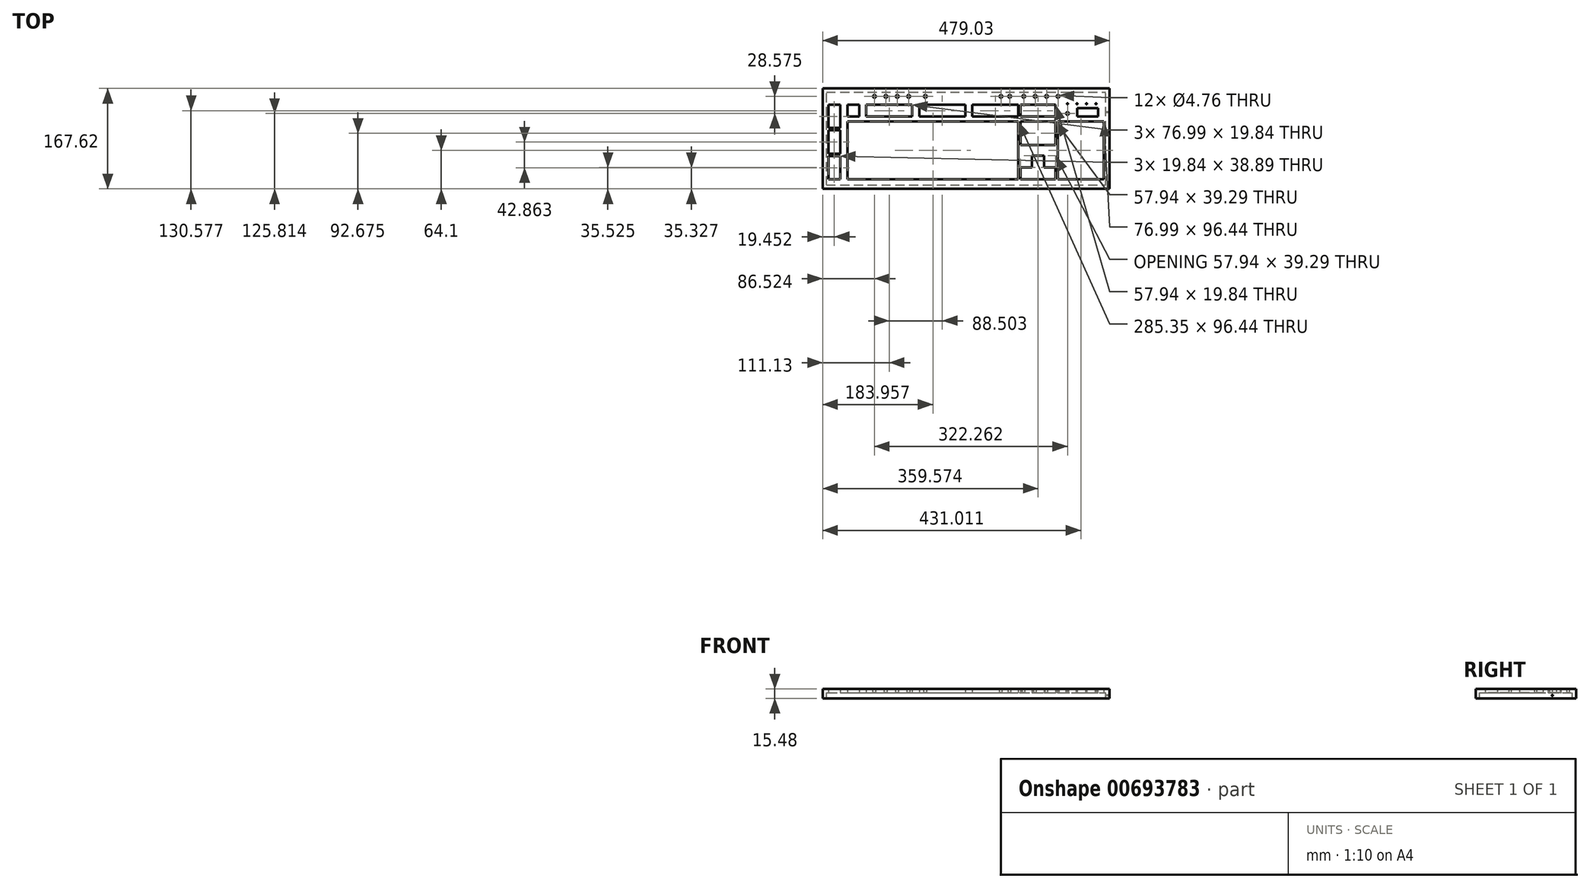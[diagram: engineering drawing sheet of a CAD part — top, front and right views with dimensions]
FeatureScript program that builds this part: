
annotation { "Feature Type Name" : "Feature", "Feature Type Description" : "" }
export const myFeature = defineFeature(function(context is Context, id is Id, definition is map)
    precondition{}
    {
        {
            var Q0;
            Q0=qCreatedBy(makeId("Top.planeOp"),FACE);
            var sketch = newSketch(context, id + "F0", { "sketchPlane" : qUnion([Q0])});
            skLineSegment(sketch, "E0.bottom", {"start": v(6.35, 6.35) * mm, "end": v(26.2, 6.35) * mm});
            skLineSegment(sketch, "E0.top", {"start": v(6.35, 45.24) * mm, "end": v(26.2, 45.24) * mm});
            skLineSegment(sketch, "E0.left", {"start": v(6.35, 6.35) * mm, "end": v(6.35, 45.24) * mm});
            skLineSegment(sketch, "E0.right", {"start": v(26.2, 6.35) * mm, "end": v(26.2, 45.24) * mm});
            skLineSegment(sketch, "E1.bottom", {"start": v(6.35, 49.21) * mm, "end": v(26.2, 49.21) * mm});
            skLineSegment(sketch, "E1.top", {"start": v(6.35, 88.1) * mm, "end": v(26.2, 88.1) * mm});
            skLineSegment(sketch, "E1.left", {"start": v(6.35, 49.21) * mm, "end": v(6.35, 88.1) * mm});
            skLineSegment(sketch, "E1.right", {"start": v(26.2, 49.21) * mm, "end": v(26.2, 88.1) * mm});
            skLineSegment(sketch, "E2.bottom", {"start": v(6.35, 92.08) * mm, "end": v(26.2, 92.08) * mm});
            skLineSegment(sketch, "E2.top", {"start": v(6.35, 130.97) * mm, "end": v(26.2, 130.97) * mm});
            skLineSegment(sketch, "E2.left", {"start": v(6.35, 92.08) * mm, "end": v(6.35, 130.97) * mm});
            skLineSegment(sketch, "E2.right", {"start": v(26.2, 92.08) * mm, "end": v(26.2, 130.97) * mm});
            skLineSegment(sketch, "E3.bottom", {"start": v(38.1, 130.97) * mm, "end": v(57.94, 130.97) * mm});
            skLineSegment(sketch, "E3.top", {"start": v(38.1, 111.13) * mm, "end": v(57.94, 111.13) * mm});
            skLineSegment(sketch, "E3.left", {"start": v(38.1, 130.97) * mm, "end": v(38.1, 111.13) * mm});
            skLineSegment(sketch, "E3.right", {"start": v(57.94, 130.97) * mm, "end": v(57.94, 111.13) * mm});
            skLineSegment(sketch, "E4.bottom", {"start": v(69.45, 111.13) * mm, "end": v(146.45, 111.13) * mm});
            skLineSegment(sketch, "E4.top", {"start": v(69.45, 130.97) * mm, "end": v(146.45, 130.97) * mm});
            skLineSegment(sketch, "E4.left", {"start": v(69.45, 111.13) * mm, "end": v(69.45, 130.97) * mm});
            skLineSegment(sketch, "E4.right", {"start": v(146.45, 111.13) * mm, "end": v(146.45, 130.97) * mm});
            skLineSegment(sketch, "E5.bottom", {"start": v(157.96, 130.97) * mm, "end": v(234.95, 130.97) * mm});
            skLineSegment(sketch, "E5.top", {"start": v(157.96, 111.13) * mm, "end": v(234.95, 111.13) * mm});
            skLineSegment(sketch, "E5.left", {"start": v(157.96, 130.97) * mm, "end": v(157.96, 111.13) * mm});
            skLineSegment(sketch, "E5.right", {"start": v(234.95, 130.97) * mm, "end": v(234.95, 111.13) * mm});
            skLineSegment(sketch, "E6.bottom", {"start": v(246.46, 111.13) * mm, "end": v(323.45, 111.13) * mm});
            skLineSegment(sketch, "E6.top", {"start": v(246.46, 130.97) * mm, "end": v(323.45, 130.97) * mm});
            skLineSegment(sketch, "E6.left", {"start": v(246.46, 111.13) * mm, "end": v(246.46, 130.97) * mm});
            skLineSegment(sketch, "E6.right", {"start": v(323.45, 111.13) * mm, "end": v(323.45, 130.97) * mm});
            skLineSegment(sketch, "E7.bottom", {"start": v(38.1, 6.35) * mm, "end": v(323.45, 6.35) * mm});
            skLineSegment(sketch, "E7.top", {"start": v(38.1, 102.8) * mm, "end": v(323.45, 102.8) * mm});
            skLineSegment(sketch, "E7.left", {"start": v(38.1, 6.35) * mm, "end": v(38.1, 102.8) * mm});
            skLineSegment(sketch, "E7.right", {"start": v(323.45, 6.35) * mm, "end": v(323.45, 102.8) * mm});
            skLineSegment(sketch, "E8.bottom", {"start": v(327.42, 111.13) * mm, "end": v(385.37, 111.13) * mm});
            skLineSegment(sketch, "E8.top", {"start": v(327.42, 130.97) * mm, "end": v(385.37, 130.97) * mm});
            skLineSegment(sketch, "E8.left", {"start": v(327.42, 111.13) * mm, "end": v(327.42, 130.97) * mm});
            skLineSegment(sketch, "E8.right", {"start": v(385.37, 111.13) * mm, "end": v(385.37, 130.97) * mm});
            skLineSegment(sketch, "E9.bottom", {"start": v(327.42, 102.8) * mm, "end": v(385.37, 102.8) * mm});
            skLineSegment(sketch, "E9.top", {"start": v(327.42, 63.5) * mm, "end": v(385.37, 63.5) * mm});
            skLineSegment(sketch, "E9.left", {"start": v(327.42, 102.8) * mm, "end": v(327.42, 63.5) * mm});
            skLineSegment(sketch, "E9.right", {"start": v(385.37, 102.8) * mm, "end": v(385.37, 63.5) * mm});
            skLineSegment(sketch, "E10", {"start": v(327.42, 6.35) * mm, "end": v(327.42, 26.2) * mm});
            skLineSegment(sketch, "E11", {"start": v(327.42, 26.2) * mm, "end": v(346.47, 26.2) * mm});
            skLineSegment(sketch, "E12", {"start": v(346.47, 26.2) * mm, "end": v(346.47, 45.64) * mm});
            skLineSegment(sketch, "E13", {"start": v(346.47, 45.64) * mm, "end": v(366.32, 45.64) * mm});
            skLineSegment(sketch, "E14", {"start": v(366.32, 45.64) * mm, "end": v(366.32, 26.2) * mm});
            skLineSegment(sketch, "E15", {"start": v(366.32, 26.2) * mm, "end": v(385.37, 26.2) * mm});
            skLineSegment(sketch, "E16", {"start": v(385.37, 26.2) * mm, "end": v(385.37, 6.35) * mm});
            skLineSegment(sketch, "E17", {"start": v(385.37, 6.35) * mm, "end": v(327.42, 6.35) * mm});
            skPoint(sketch, "E18", {"position": v(356.4, 6.35) * mm});
            skPoint(sketch, "E19", {"position": v(356.4, 45.64) * mm});
            skLineSegment(sketch, "E20.bottom", {"start": v(389.33, 6.35) * mm, "end": v(466.33, 6.35) * mm});
            skLineSegment(sketch, "E20.top", {"start": v(389.33, 102.8) * mm, "end": v(466.33, 102.8) * mm});
            skLineSegment(sketch, "E20.left", {"start": v(389.33, 6.35) * mm, "end": v(389.33, 102.8) * mm});
            skLineSegment(sketch, "E20.right", {"start": v(466.33, 6.35) * mm, "end": v(466.33, 102.8) * mm});
            skLineSegment(sketch, "E21.bottom", {"start": v(-3.18, -9.53) * mm, "end": v(475.85, -9.52) * mm});
            skLineSegment(sketch, "E21.top", {"start": v(-3.18, 158.1) * mm, "end": v(475.85, 158.1) * mm});
            skLineSegment(sketch, "E21.left", {"start": v(-3.18, -9.53) * mm, "end": v(-3.18, 158.1) * mm});
            skLineSegment(sketch, "E21.right", {"start": v(475.85, -9.52) * mm, "end": v(475.85, 158.1) * mm});
            skSolve(sketch);
        }
        {
            var Q0;
            Q0 = qSketchRegion(id + "F0", true);
            extrude(context, id + "F1", {"entities" : qUnion([Q0]), "depth" : 5.95 * mm, "offsetDistance" : 25.4 * mm});
        }
        {
            var Q0;
            Q0=makeQuery(id+"F1.opExtrude","CAP_FACE",FACE,{"disambiguationData":[OSD([sQuery(id+"F0.wireOp",EDGE,"PK97KQgg-SKCG-tWN8-NHXi-s2q7hArUiRFD"),sQuery(id+"F0.wireOp",EDGE,"YormQwom-BUWa-J8ki-09Gs-298X1OSeOC6b"),sQuery(id+"F0.wireOp",EDGE,"seqywk22-XLSG-NzTa-OlvC-Va2yxN94JzAi"),sQuery(id+"F0.wireOp",EDGE,"E0.bottom"),sQuery(id+"F0.wireOp",EDGE,"E0.top"),sQuery(id+"F0.wireOp",EDGE,"E0.left"),sQuery(id+"F0.wireOp",EDGE,"E0.right"),sQuery(id+"F0.wireOp",EDGE,"E1.bottom"),sQuery(id+"F0.wireOp",EDGE,"E1.top"),sQuery(id+"F0.wireOp",EDGE,"E1.left"),sQuery(id+"F0.wireOp",EDGE,"E1.right"),sQuery(id+"F0.wireOp",EDGE,"E2.bottom"),sQuery(id+"F0.wireOp",EDGE,"E2.top"),sQuery(id+"F0.wireOp",EDGE,"E2.left"),sQuery(id+"F0.wireOp",EDGE,"E2.right"),sQuery(id+"F0.wireOp",EDGE,"E3.bottom"),sQuery(id+"F0.wireOp",EDGE,"E3.top"),sQuery(id+"F0.wireOp",EDGE,"E3.left"),sQuery(id+"F0.wireOp",EDGE,"E3.right"),sQuery(id+"F0.wireOp",EDGE,"E4.bottom"),sQuery(id+"F0.wireOp",EDGE,"E4.top"),sQuery(id+"F0.wireOp",EDGE,"E4.left"),sQuery(id+"F0.wireOp",EDGE,"E4.right"),sQuery(id+"F0.wireOp",EDGE,"E5.bottom"),sQuery(id+"F0.wireOp",EDGE,"E5.top"),sQuery(id+"F0.wireOp",EDGE,"E5.left"),sQuery(id+"F0.wireOp",EDGE,"E5.right"),sQuery(id+"F0.wireOp",EDGE,"E6.bottom"),sQuery(id+"F0.wireOp",EDGE,"E6.top"),sQuery(id+"F0.wireOp",EDGE,"E6.left"),sQuery(id+"F0.wireOp",EDGE,"E6.right"),sQuery(id+"F0.wireOp",EDGE,"E7.bottom"),sQuery(id+"F0.wireOp",EDGE,"E7.top"),sQuery(id+"F0.wireOp",EDGE,"E7.left"),sQuery(id+"F0.wireOp",EDGE,"E7.right"),sQuery(id+"F0.wireOp",EDGE,"E8.bottom"),sQuery(id+"F0.wireOp",EDGE,"E8.top"),sQuery(id+"F0.wireOp",EDGE,"E8.left"),sQuery(id+"F0.wireOp",EDGE,"E8.right"),sQuery(id+"F0.wireOp",EDGE,"E9.bottom"),sQuery(id+"F0.wireOp",EDGE,"E9.top"),sQuery(id+"F0.wireOp",EDGE,"E9.left"),sQuery(id+"F0.wireOp",EDGE,"E9.right"),sQuery(id+"F0.wireOp",EDGE,"E10"),sQuery(id+"F0.wireOp",EDGE,"E11"),sQuery(id+"F0.wireOp",EDGE,"E12"),sQuery(id+"F0.wireOp",EDGE,"E13"),sQuery(id+"F0.wireOp",EDGE,"E14"),sQuery(id+"F0.wireOp",EDGE,"E15"),sQuery(id+"F0.wireOp",EDGE,"E16"),sQuery(id+"F0.wireOp",EDGE,"E17"),sQuery(id+"F0.wireOp",EDGE,"E20.bottom"),sQuery(id+"F0.wireOp",EDGE,"E20.top"),sQuery(id+"F0.wireOp",EDGE,"E20.left"),sQuery(id+"F0.wireOp",EDGE,"E20.right"),sQuery(id+"F0.wireOp",EDGE,"CHscRm9Q-nY2i-4dEZ-vLJR-UmYNDSLBzwNv"),sQuery(id+"F0.wireOp",EDGE,"pIAb1olm-O37X-Hfz9-O6eL-bn9l9E0TeTdk"),sQuery(id+"F0.wireOp",EDGE,"JB2mssER-Nrez-Saej-cGK4-Emf1xQ05upFG"),sQuery(id+"F0.wireOp",EDGE,"QgIi0HC4-owDL-alPb-fxt3-70y0Pu92cPBn")])],"isStart":false});
            var sketch = newSketch(context, id + "F2", { "sketchPlane" : qUnion([Q0])});
            skCircle(sketch, "E22", {"center": v(83.34, 144.86) * mm, "radius": 2.38 * mm});
            skCircle(sketch, "E23", {"center": v(102.4, 144.86) * mm, "radius": 2.38 * mm});
            skCircle(sketch, "E24", {"center": v(121.44, 144.86) * mm, "radius": 2.38 * mm});
            skCircle(sketch, "E25", {"center": v(140.5, 144.86) * mm, "radius": 2.38 * mm});
            skCircle(sketch, "E26", {"center": v(168.27, 144.86) * mm, "radius": 2.38 * mm});
            skCircle(sketch, "E27", {"center": v(294.48, 144.86) * mm, "radius": 2.38 * mm});
            skCircle(sketch, "E28", {"center": v(309.17, 144.86) * mm, "radius": 2.38 * mm});
            skCircle(sketch, "E29", {"center": v(332.58, 144.86) * mm, "radius": 2.38 * mm});
            skCircle(sketch, "E30", {"center": v(351.63, 144.86) * mm, "radius": 2.38 * mm});
            skCircle(sketch, "E31", {"center": v(370.68, 144.86) * mm, "radius": 2.38 * mm});
            skCircle(sketch, "E32", {"center": v(389.73, 144.86) * mm, "radius": 2.38 * mm});
            skCircle(sketch, "E33", {"center": v(405.6, 116.28) * mm, "radius": 2.38 * mm});
            skCircle(sketch, "E34", {"center": v(405.6, 132.56) * mm, "radius": 0.8 * mm});
            skCircle(sketch, "E35", {"center": v(421.48, 132.56) * mm, "radius": 0.8 * mm});
            skCircle(sketch, "E36", {"center": v(437.36, 132.56) * mm, "radius": 0.8 * mm});
            skCircle(sketch, "E37", {"center": v(453.23, 132.56) * mm, "radius": 0.8 * mm});
            skSolve(sketch);
        }
        {
            var Q0;
            Q0 = qSketchRegion(id + "F2", true);
            extrude(context, id + "F3", {"entities" : qUnion([Q0]), "operationType" : NewBodyOperationType.REMOVE, "endBound" : BoundingType.THROUGH_ALL, "oppositeDirection" : true, "depth" : 25.4 * mm, "offsetDistance" : 25.4 * mm});
        }
        {
            var Q0;
            Q0=makeQuery(id+"F1.opExtrude","CAP_FACE",FACE,{"disambiguationData":[OSD([sQuery(id+"F0.wireOp",EDGE,"E0.bottom"),sQuery(id+"F0.wireOp",EDGE,"E0.top"),sQuery(id+"F0.wireOp",EDGE,"E0.left"),sQuery(id+"F0.wireOp",EDGE,"E0.right"),sQuery(id+"F0.wireOp",EDGE,"E1.bottom"),sQuery(id+"F0.wireOp",EDGE,"E1.top"),sQuery(id+"F0.wireOp",EDGE,"E1.left"),sQuery(id+"F0.wireOp",EDGE,"E1.right"),sQuery(id+"F0.wireOp",EDGE,"E2.bottom"),sQuery(id+"F0.wireOp",EDGE,"E2.top"),sQuery(id+"F0.wireOp",EDGE,"E2.left"),sQuery(id+"F0.wireOp",EDGE,"E2.right"),sQuery(id+"F0.wireOp",EDGE,"E3.bottom"),sQuery(id+"F0.wireOp",EDGE,"E3.top"),sQuery(id+"F0.wireOp",EDGE,"E3.left"),sQuery(id+"F0.wireOp",EDGE,"E3.right"),sQuery(id+"F0.wireOp",EDGE,"E4.bottom"),sQuery(id+"F0.wireOp",EDGE,"E4.top"),sQuery(id+"F0.wireOp",EDGE,"E4.left"),sQuery(id+"F0.wireOp",EDGE,"E4.right"),sQuery(id+"F0.wireOp",EDGE,"E5.bottom"),sQuery(id+"F0.wireOp",EDGE,"E5.top"),sQuery(id+"F0.wireOp",EDGE,"E5.left"),sQuery(id+"F0.wireOp",EDGE,"E5.right"),sQuery(id+"F0.wireOp",EDGE,"E6.bottom"),sQuery(id+"F0.wireOp",EDGE,"E6.top"),sQuery(id+"F0.wireOp",EDGE,"E6.left"),sQuery(id+"F0.wireOp",EDGE,"E6.right"),sQuery(id+"F0.wireOp",EDGE,"E7.bottom"),sQuery(id+"F0.wireOp",EDGE,"E7.top"),sQuery(id+"F0.wireOp",EDGE,"E7.left"),sQuery(id+"F0.wireOp",EDGE,"E7.right"),sQuery(id+"F0.wireOp",EDGE,"E8.bottom"),sQuery(id+"F0.wireOp",EDGE,"E8.top"),sQuery(id+"F0.wireOp",EDGE,"E8.left"),sQuery(id+"F0.wireOp",EDGE,"E8.right"),sQuery(id+"F0.wireOp",EDGE,"E9.bottom"),sQuery(id+"F0.wireOp",EDGE,"E9.top"),sQuery(id+"F0.wireOp",EDGE,"E9.left"),sQuery(id+"F0.wireOp",EDGE,"E9.right"),sQuery(id+"F0.wireOp",EDGE,"E10"),sQuery(id+"F0.wireOp",EDGE,"E11"),sQuery(id+"F0.wireOp",EDGE,"E12"),sQuery(id+"F0.wireOp",EDGE,"E13"),sQuery(id+"F0.wireOp",EDGE,"E14"),sQuery(id+"F0.wireOp",EDGE,"E15"),sQuery(id+"F0.wireOp",EDGE,"E16"),sQuery(id+"F0.wireOp",EDGE,"E17"),sQuery(id+"F0.wireOp",EDGE,"E20.bottom"),sQuery(id+"F0.wireOp",EDGE,"E20.top"),sQuery(id+"F0.wireOp",EDGE,"E20.left"),sQuery(id+"F0.wireOp",EDGE,"E20.right"),sQuery(id+"F0.wireOp",EDGE,"E21.bottom"),sQuery(id+"F0.wireOp",EDGE,"E21.top"),sQuery(id+"F0.wireOp",EDGE,"E21.left"),sQuery(id+"F0.wireOp",EDGE,"E21.right")])],"isStart":true});
            var sketch = newSketch(context, id + "F4", { "sketchPlane" : qUnion([Q0])});
            skLineSegment(sketch, "E38.bottom", {"start": v(-3.18, 9.53) * mm, "end": v(475.85, 9.53) * mm});
            skLineSegment(sketch, "E38.top", {"start": v(-3.18, -158.1) * mm, "end": v(475.85, -158.1) * mm});
            skLineSegment(sketch, "E38.left", {"start": v(-3.18, 9.53) * mm, "end": v(-3.18, -158.1) * mm});
            skLineSegment(sketch, "E38.right", {"start": v(475.85, 9.53) * mm, "end": v(475.85, -158.1) * mm});
            skLineSegment(sketch, "E39.bottom", {"start": v(3.17, 3.18) * mm, "end": v(469.5, 3.18) * mm});
            skLineSegment(sketch, "E39.top", {"start": v(3.18, -151.74) * mm, "end": v(469.5, -151.74) * mm});
            skLineSegment(sketch, "E39.left", {"start": v(3.17, 3.18) * mm, "end": v(3.17, -151.74) * mm});
            skLineSegment(sketch, "E39.right", {"start": v(469.5, 3.18) * mm, "end": v(469.5, -151.74) * mm});
            skSolve(sketch);
        }
        {
            var Q0;
            Q0 = qSketchRegion(id + "F4", true);
            extrude(context, id + "F5", {"entities" : qUnion([Q0]), "operationType" : NewBodyOperationType.ADD, "depth" : 9.52 * mm, "offsetDistance" : 25.4 * mm});
        }
        {
            var Q0;
            Q0=makeQuery(id+"F1.opExtrude","CAP_FACE",FACE,{"disambiguationData":[OSD([sQuery(id+"F0.wireOp",EDGE,"E0.bottom"),sQuery(id+"F0.wireOp",EDGE,"E0.top"),sQuery(id+"F0.wireOp",EDGE,"E0.left"),sQuery(id+"F0.wireOp",EDGE,"E0.right"),sQuery(id+"F0.wireOp",EDGE,"E1.bottom"),sQuery(id+"F0.wireOp",EDGE,"E1.top"),sQuery(id+"F0.wireOp",EDGE,"E1.left"),sQuery(id+"F0.wireOp",EDGE,"E1.right"),sQuery(id+"F0.wireOp",EDGE,"E2.bottom"),sQuery(id+"F0.wireOp",EDGE,"E2.top"),sQuery(id+"F0.wireOp",EDGE,"E2.left"),sQuery(id+"F0.wireOp",EDGE,"E2.right"),sQuery(id+"F0.wireOp",EDGE,"E3.bottom"),sQuery(id+"F0.wireOp",EDGE,"E3.top"),sQuery(id+"F0.wireOp",EDGE,"E3.left"),sQuery(id+"F0.wireOp",EDGE,"E3.right"),sQuery(id+"F0.wireOp",EDGE,"E4.bottom"),sQuery(id+"F0.wireOp",EDGE,"E4.top"),sQuery(id+"F0.wireOp",EDGE,"E4.left"),sQuery(id+"F0.wireOp",EDGE,"E4.right"),sQuery(id+"F0.wireOp",EDGE,"E5.bottom"),sQuery(id+"F0.wireOp",EDGE,"E5.top"),sQuery(id+"F0.wireOp",EDGE,"E5.left"),sQuery(id+"F0.wireOp",EDGE,"E5.right"),sQuery(id+"F0.wireOp",EDGE,"E6.bottom"),sQuery(id+"F0.wireOp",EDGE,"E6.top"),sQuery(id+"F0.wireOp",EDGE,"E6.left"),sQuery(id+"F0.wireOp",EDGE,"E6.right"),sQuery(id+"F0.wireOp",EDGE,"E7.bottom"),sQuery(id+"F0.wireOp",EDGE,"E7.top"),sQuery(id+"F0.wireOp",EDGE,"E7.left"),sQuery(id+"F0.wireOp",EDGE,"E7.right"),sQuery(id+"F0.wireOp",EDGE,"E8.bottom"),sQuery(id+"F0.wireOp",EDGE,"E8.top"),sQuery(id+"F0.wireOp",EDGE,"E8.left"),sQuery(id+"F0.wireOp",EDGE,"E8.right"),sQuery(id+"F0.wireOp",EDGE,"E9.bottom"),sQuery(id+"F0.wireOp",EDGE,"E9.top"),sQuery(id+"F0.wireOp",EDGE,"E9.left"),sQuery(id+"F0.wireOp",EDGE,"E9.right"),sQuery(id+"F0.wireOp",EDGE,"E10"),sQuery(id+"F0.wireOp",EDGE,"E11"),sQuery(id+"F0.wireOp",EDGE,"E12"),sQuery(id+"F0.wireOp",EDGE,"E13"),sQuery(id+"F0.wireOp",EDGE,"E14"),sQuery(id+"F0.wireOp",EDGE,"E15"),sQuery(id+"F0.wireOp",EDGE,"E16"),sQuery(id+"F0.wireOp",EDGE,"E17"),sQuery(id+"F0.wireOp",EDGE,"E20.bottom"),sQuery(id+"F0.wireOp",EDGE,"E20.top"),sQuery(id+"F0.wireOp",EDGE,"E20.left"),sQuery(id+"F0.wireOp",EDGE,"E20.right"),sQuery(id+"F0.wireOp",EDGE,"E21.bottom"),sQuery(id+"F0.wireOp",EDGE,"E21.top"),sQuery(id+"F0.wireOp",EDGE,"E21.left"),sQuery(id+"F0.wireOp",EDGE,"E21.right")])],"isStart":false});
            var sketch = newSketch(context, id + "F6", { "sketchPlane" : qUnion([Q0])});
            skLineSegment(sketch, "E40.bottom", {"start": v(421.88, 125.41) * mm, "end": v(456.8, 125.41) * mm});
            skLineSegment(sketch, "E40.top", {"start": v(421.88, 111.13) * mm, "end": v(456.8, 111.13) * mm});
            skLineSegment(sketch, "E40.left", {"start": v(421.88, 125.41) * mm, "end": v(421.88, 111.13) * mm});
            skLineSegment(sketch, "E40.right", {"start": v(456.8, 125.41) * mm, "end": v(456.8, 111.13) * mm});
            skSolve(sketch);
        }
        {
            var Q0;
            Q0 = qSketchRegion(id + "F6", true);
            extrude(context, id + "F7", {"entities" : qUnion([Q0]), "operationType" : NewBodyOperationType.REMOVE, "endBound" : BoundingType.THROUGH_ALL, "oppositeDirection" : true, "depth" : 25.4 * mm, "offsetDistance" : 25.4 * mm});
        }
        {
            var Q0;
            Q0=qCreatedBy(makeId("Right.planeOp"),FACE);
            cPlane(context, id + "F8", {"entities" : qUnion([Q0]), "cplaneType" : CPlaneType.OFFSET, "offset" : 433.32 * mm, "width" : 152.4 * mm, "height" : 152.4 * mm});
        }
        {
            var Q0;
            Q0=qCreatedBy(id+"F8.planeOp",FACE);
            var sketch = newSketch(context, id + "F9", { "sketchPlane" : qUnion([Q0])});
            skCircle(sketch, "E41", {"center": v(118.27, -4.76) * mm, "radius": 0.8 * mm});
            skPoint(sketch, "E42", {"position": v(118.27, 0) * mm});
            skSolve(sketch);
        }
        {
            var Q0;
            Q0 = qSketchRegion(id + "F9", true);
            extrude(context, id + "F10", {"entities" : qUnion([Q0]), "operationType" : NewBodyOperationType.REMOVE, "endBound" : BoundingType.THROUGH_ALL, "depth" : 25.4 * mm, "offsetDistance" : 25.4 * mm});
        }
    });
